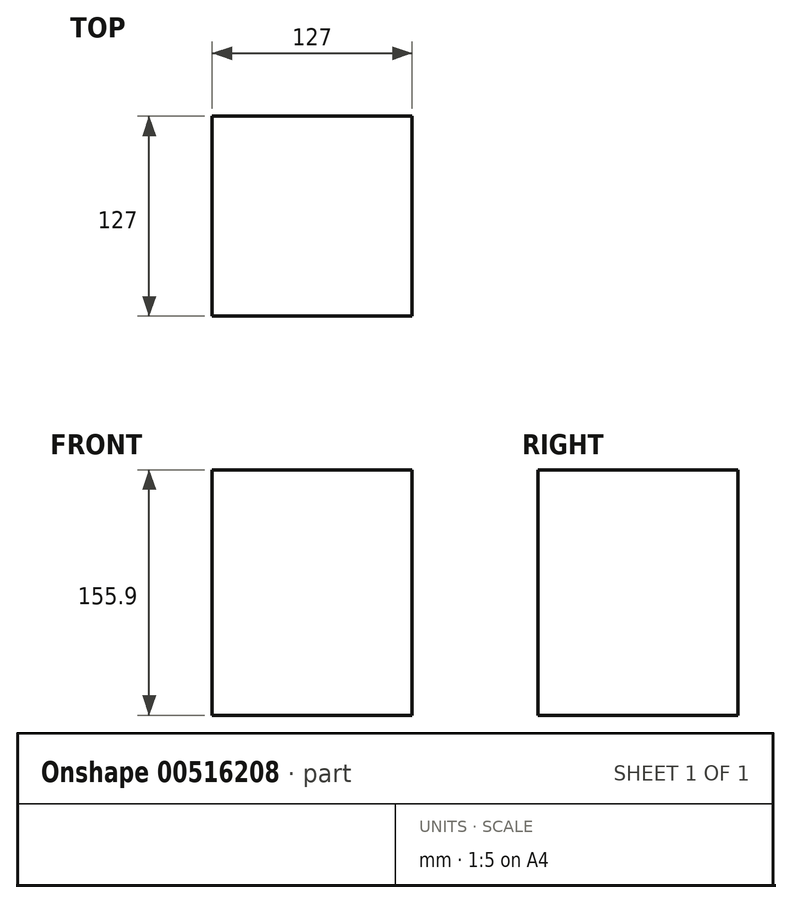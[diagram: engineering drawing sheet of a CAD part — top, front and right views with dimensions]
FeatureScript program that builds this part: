
annotation { "Feature Type Name" : "Feature", "Feature Type Description" : "" }
export const myFeature = defineFeature(function(context is Context, id is Id, definition is map)
    precondition{}
    {
        {
            var Q0;
            Q0=qCreatedBy(makeId("Front.planeOp"),FACE);
            var sketch = newSketch(context, id + "F0", { "sketchPlane" : qUnion([Q0])});
            skLineSegment(sketch, "E0.bottom", {"start": v(-63.5, 77.95) * mm, "end": v(63.5, 77.95) * mm});
            skLineSegment(sketch, "E0.top", {"start": v(-63.5, -77.95) * mm, "end": v(63.5, -77.95) * mm});
            skLineSegment(sketch, "E0.left", {"start": v(-63.5, 77.95) * mm, "end": v(-63.5, -77.95) * mm});
            skLineSegment(sketch, "E0.right", {"start": v(63.5, 77.95) * mm, "end": v(63.5, -77.95) * mm});
            skSolve(sketch);
        }
        {
            var Q0;
            Q0=makeQuery(id+"F0.imprint","IMPRINT",FACE,{"disambiguationData":[TD([[makeQuery(id+"F0.imprint","IMPRINT",EDGE,{"derivedFrom":sQuery(id+"F0.wireOp",EDGE,"E0.bottom")}),-1.0]])]});
            extrude(context, id + "F1", {"entities" : qUnion([Q0]), "depth" : 127 * mm, "offsetDistance" : 25.4 * mm});
        }
    });
